# Revit family: PRD_FrankeWS_SftyShwrs_EmergencyShower_FAID0008
name_source: partatom
category: Plumbing Fixtures
revit_build: Autodesk Revit 2018 (Build: 20190510_1515(x64)
units: mm (PartAtom-declared; Revit-internal decimal feet)

## family parameters
Cut with Voids When Loaded = Yes
Host = Face
OmniClass Number = 23.45.05.14.99
OmniClass Title = Other Sanitary Washing Plumbing Fixtures
Part Type = Normal
Room Calculation Point = No
Round Connector Dimension = Use Diameter
Shared = Yes

## types (1)
- FAID0008
    AssetType = Fixed
    BIMObjectName = PRD_AR_SafetyShowers_EmergencyShower_FAID0008
    Category = Pr_40_20_27_75, Safety showers
    Color = green
    Default Elevation = 2300 mm
    Description = Pull-rod operated emergency shower, for surface mounting, on connection piece provided by the customer. Valve activated by triangular handle. With wall bracket and emergency shower head. Non-self-closing, the water flow is stopped by pushing up the pull rod, green EPS coating (RAL 6032), complies with EN 15154, Part 1, includes the emergency shower safety symbol on an adhesive label in compliance with ISO 3864, Part 1 and user instructions. Volumetric flow rate approx. 65 l/min at 1 bar pressure, approx. 110 l/min at 3 bar pressure, water connection G 3/4 B.
    DiameterNominal = 20  [stored 0.0656168 ft]
    DrainSize = 20 mm  [stored 0.0656168 ft]
    DurationUnit = year
    Features = surface mounting, on connection piece provided by the customer. Valve activated by triangular handle
    Finish = EPS coated
    GrossWeight = 2.80 kg
    HasTray = FALSE
    IfcExportAs = IfcSanitaryTerminalType
    IfcExportType = SHOWER
    Manufacturer = KWC Group AG
    ManufacturerName = KWC Group AG
    ManufacturerURL = www.kwc.com
    Material = brass
    Model = FAID0008
    ModelNumber = 2030019175
    ModelReference = FAID0008
    Name = Emergency Shower FAID0008
    NetWeight = 2.10 kg
    NominalDepth = 600 mm
    NominalHeight = 0 mm  [stored 0 ft]
    NominalWidth = 0 mm  [stored 0 ft]
    ProductInformation = https://pim.kwc.com
    ShowerHeadDescription = Emergency shower head
    ShowerMaterial = PRD_AR_Brass_EPSCoated_Green
    ShowerType = Individual
    SpoutProjection = 588.00 mm
    Type = Pipe connection
    TypeOfFitting = Cantilever connection
    URL = www.kwc.com
    Uniclass2015Code = Pr_40_20_27_75
    Uniclass2015Title = Safety showers
    Uniclass2015Version = Products v1.17
    Version = 1
    VolumeFlowRate = 1.83 l/s at 3 bar
    WarrantyDurationUnit = year

note: [stored X ft] marks values corroborated as IEEE doubles in the binary element streams (Revit-internal decimal feet)

## geometry (parser evidence)
native form markers: Sweep x2
no freeform markers — native parametric forms only
